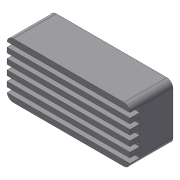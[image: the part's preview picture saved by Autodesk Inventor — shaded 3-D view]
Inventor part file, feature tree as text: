
AUTODESK INVENTOR PART (.ipt)
format: ipt  version: 2016 (Build 200138000, 138)  size: 115,200 bytes
history: native  units: in
note: dims shown in document units (in); Inventor stores cm internally (conversion verified against a paired STEP export)
features: extrude x2, sketch x2, fillet x1
ambient origin geometry x8: Origin, YZ Plane, XZ Plane, XY Plane, X Axis, Y Axis, Z Axis, Center Point
bodies: Solid1 (feature_tree)
feature tree (5):
  extrude  "Extrusion1"  Depth=1.125in
  fillet  "Fillet1"  Radius=0.875in
  extrude  "Extrusion2"  Depth=0.1in
  sketch  "Sketch1"  dims[d0=2.5in d1=1.125in d2=0.875in d3=0.0in]
  sketch  "Sketch2"  dims[d4=0.125in d5=0.1in d6=1.9685in d8=0.2in d9=0.3937in d11=1.0in d13=0.2in d14=0.0in]
